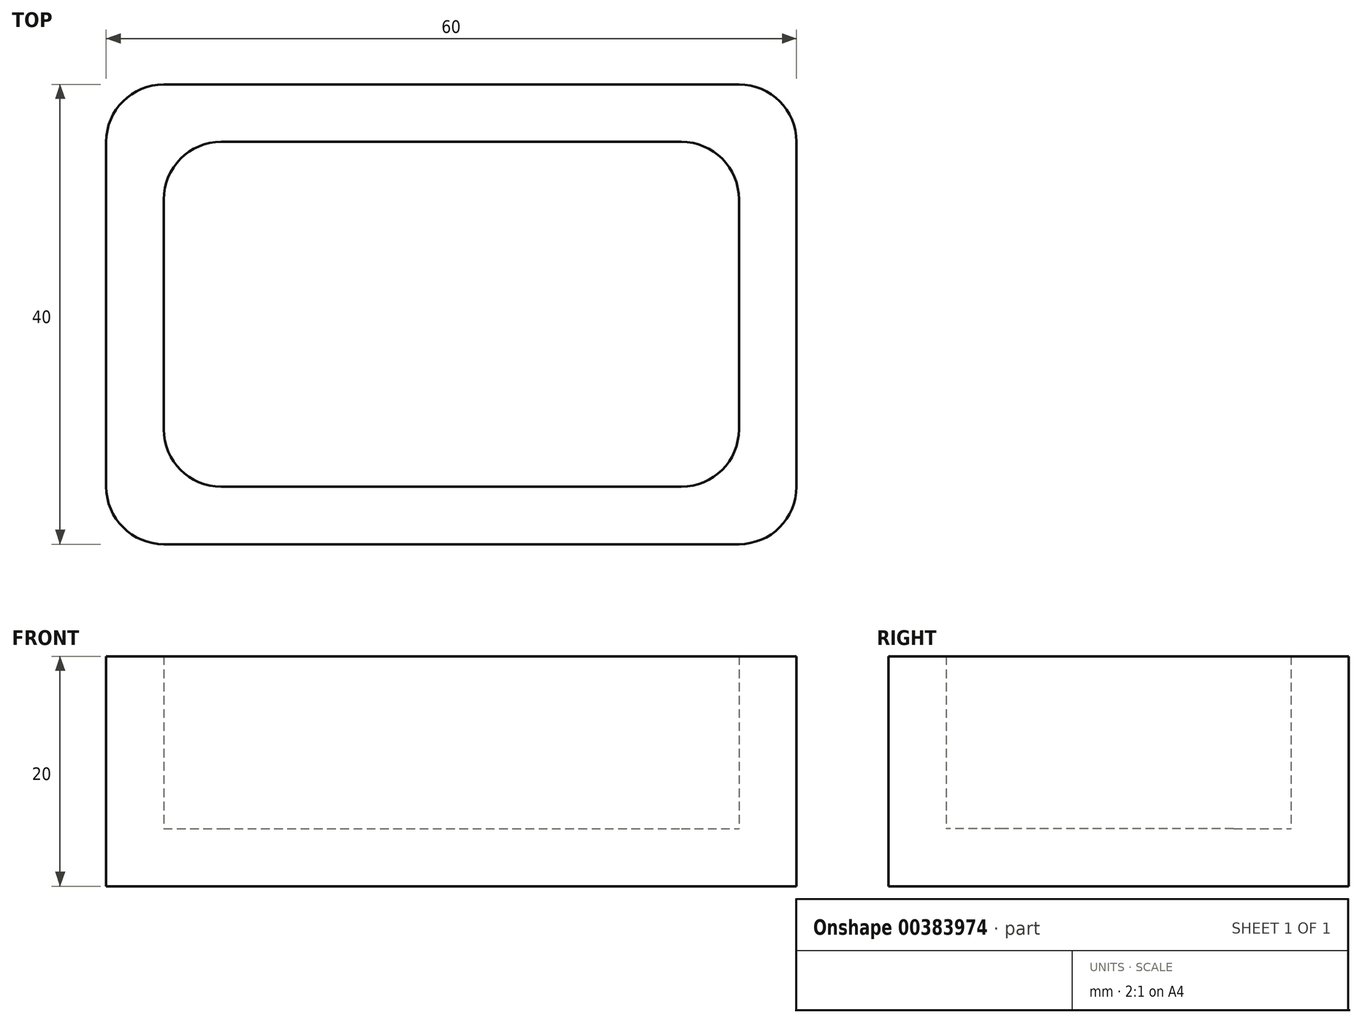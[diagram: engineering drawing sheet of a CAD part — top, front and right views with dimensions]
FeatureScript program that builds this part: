
annotation { "Feature Type Name" : "Feature", "Feature Type Description" : "" }
export const myFeature = defineFeature(function(context is Context, id is Id, definition is map)
    precondition{}
    {
        {
            var Q0;
            Q0=qCreatedBy(makeId("Top.planeOp"),FACE);
            var sketch = newSketch(context, id + "F0", { "sketchPlane" : qUnion([Q0])});
            skLineSegment(sketch, "E0.bottom", {"start": v(-30, 20) * mm, "end": v(30, 20) * mm});
            skLineSegment(sketch, "E0.top", {"start": v(-30, -20) * mm, "end": v(30, -20) * mm});
            skLineSegment(sketch, "E0.left", {"start": v(-30, 20) * mm, "end": v(-30, -20) * mm});
            skLineSegment(sketch, "E0.right", {"start": v(30, 20) * mm, "end": v(30, -20) * mm});
            skPoint(sketch, "E0.middle", {"position": v(0, 0) * mm});
            skSolve(sketch);
        }
        {
            var Q0;
            Q0=qSketchRegion(id+"F0",true);
            extrude(context, id + "F1", {"entities" : qUnion([Q0]), "depth" : 15 * mm});
        }
        {
            var Q0;
            Q0=makeQuery(id+"F1.opExtrude","CAP_FACE",FACE,{"disambiguationData":[OSD([sQuery(id+"F0.wireOp",EDGE,"E0.bottom"),sQuery(id+"F0.wireOp",EDGE,"E0.top"),sQuery(id+"F0.wireOp",EDGE,"E0.left"),sQuery(id+"F0.wireOp",EDGE,"E0.right")])],"isStart":false});
            extrude(context, id + "F2", {"entities" : qUnion([Q0]), "operationType" : NewBodyOperationType.ADD, "depth" : 5 * mm});
        }
        {
            var Q0;
            Q0=makeQuery(id+"F2.opExtrude","CAP_FACE",FACE,{"disambiguationData":[OSD([sQuery(id+"F0.wireOp",EDGE,"E0.bottom"),sQuery(id+"F0.wireOp",EDGE,"E0.top"),sQuery(id+"F0.wireOp",EDGE,"E0.left"),sQuery(id+"F0.wireOp",EDGE,"E0.right")])],"isStart":false});
            shell(context, id + "F3", {"entities" : qUnion([Q0]), "thickness" : 5 * mm});
        }
        {
            var Q0;
            {var subQ0=sQuery(id+"F0.wireOp",EDGE,"E0.left");var subQ1=sQuery(id+"F0.wireOp",EDGE,"E0.bottom");Q0=makeQuery(id+"F2.boolean.opBoolean","MERGE",EDGE,{"derivedFrom":[makeQuery(id+"F1.opExtrude","SWEPT_EDGE",EDGE,{"disambiguationData":[OSD([subQ1,subQ0])]}),makeQuery(id+"F2.opExtrude","SWEPT_EDGE",EDGE,{"disambiguationData":[OSD([subQ1,subQ0])]})]});}
            var Q1;
            {var subQ0=sQuery(id+"F0.wireOp",EDGE,"E0.left");var subQ1=sQuery(id+"F0.wireOp",EDGE,"E0.top");Q1=makeQuery(id+"F2.boolean.opBoolean","MERGE",EDGE,{"derivedFrom":[makeQuery(id+"F1.opExtrude","SWEPT_EDGE",EDGE,{"disambiguationData":[OSD([subQ1,subQ0])]}),makeQuery(id+"F2.opExtrude","SWEPT_EDGE",EDGE,{"disambiguationData":[OSD([subQ1,subQ0])]})]});}
            var Q2;
            {var subQ0=sQuery(id+"F0.wireOp",EDGE,"E0.right");var subQ1=sQuery(id+"F0.wireOp",EDGE,"E0.top");Q2=makeQuery(id+"F2.boolean.opBoolean","MERGE",EDGE,{"derivedFrom":[makeQuery(id+"F1.opExtrude","SWEPT_EDGE",EDGE,{"disambiguationData":[OSD([subQ1,subQ0])]}),makeQuery(id+"F2.opExtrude","SWEPT_EDGE",EDGE,{"disambiguationData":[OSD([subQ1,subQ0])]})]});}
            var Q3;
            {var subQ0=sQuery(id+"F0.wireOp",EDGE,"E0.right");var subQ1=sQuery(id+"F0.wireOp",EDGE,"E0.bottom");Q3=makeQuery(id+"F2.boolean.opBoolean","MERGE",EDGE,{"derivedFrom":[makeQuery(id+"F1.opExtrude","SWEPT_EDGE",EDGE,{"disambiguationData":[OSD([subQ1,subQ0])]}),makeQuery(id+"F2.opExtrude","SWEPT_EDGE",EDGE,{"disambiguationData":[OSD([subQ1,subQ0])]})]});}
            var Q4;
            Q4=makeQuery(id+"F3.opShell","OFFSET_EDGE",EDGE,{"disambiguationData":[OSD([sQuery(id+"F0.wireOp",EDGE,"E0.bottom"),sQuery(id+"F0.wireOp",EDGE,"E0.right")])]});
            var Q5;
            Q5=makeQuery(id+"F3.opShell","OFFSET_EDGE",EDGE,{"disambiguationData":[OSD([sQuery(id+"F0.wireOp",EDGE,"E0.bottom"),sQuery(id+"F0.wireOp",EDGE,"E0.left")])]});
            var Q6;
            Q6=makeQuery(id+"F3.opShell","OFFSET_EDGE",EDGE,{"disambiguationData":[OSD([sQuery(id+"F0.wireOp",EDGE,"E0.top"),sQuery(id+"F0.wireOp",EDGE,"E0.right")])]});
            var Q7;
            Q7=makeQuery(id+"F3.opShell","OFFSET_EDGE",EDGE,{"disambiguationData":[OSD([sQuery(id+"F0.wireOp",EDGE,"E0.top"),sQuery(id+"F0.wireOp",EDGE,"E0.left")])]});
            fillet(context, id + "F4", {"entities" : qUnion([Q0, Q1, Q2, Q3, Q4, Q5, Q6, Q7]), "radius" : 5 * mm, "tangentPropagation" : true, "allowEdgeOverflow" : false});
        }
    });
